# Revit family: Lighting_Linear_LED_StarTek_HydroBeam-Wall_Mount1
name_source: partatom
category: Lighting Fixtures
units: mm (PartAtom-declared; Revit-internal decimal feet)

## family parameters
Cut with Voids When Loaded = No
Host = Face
Light Source = Yes
OmniClass Number = 23.80.70.11
OmniClass Title = Luminaries for Internal Lighting
Part Type = Normal
Room Calculation Point = No
Round Connector Dimension = Use Diameter
Shared = No

## types (1)
- Not a type - Load Type Catalog!
    Apparent Load = 39 VA
    Assembly Code = D5020200
    CRI = 80
    Color Filter = 16777215
    Default Elevation = 48 "
    Description = HydroBeam
    Dimming Lamp Color Temperature Shift = <None>
    Distribution = SD
    Emit Shape Visible in Rendering = No
    Frequency = 60 Hz
    Height = 3.6 "
    Input Wattage = 36 W
    Keynote = 16500
    Lamp = LED
    Length = 60 "
    MEP Distance = 30 "
    Manufacturer = StarTek Lighting
    Number of Poles = 1
    Phase = 1
    Photometric Note = Import IES files https://starteklightingamerica.com
    Photometric Web File = Generic Light Source Shown : Please download and link the IES file that best matches your fixture specification
    Power Factor = 0.93
    Product data url = https://www.bimobject.com
    RAWM = Wall Mounting : Rigid Arm Wall Mount - RAWM
    Type Comments = Linear Lighting Fixture
    URL = https://starteklightingamerica.com
    Voltage = 120 V
    Voltage Range = 120-277V
    WM = Wall Mounting : Wall Mounted
    Wattage Comments = Efficacy up to 125 lm/W
    Weight = 0.00 lbf
    Width = 4.4 "
    z_Length 8 = No
    z_Option End = Run : End Fixture
    z_Option Middle = Run : Middle Fixture
    z_Option Standalone = Run : Standalone Fixture
    z_Option Start = Run : Start Fixture

## geometry (parser evidence)
native form markers: Sweep x9
no freeform markers — native parametric forms only
